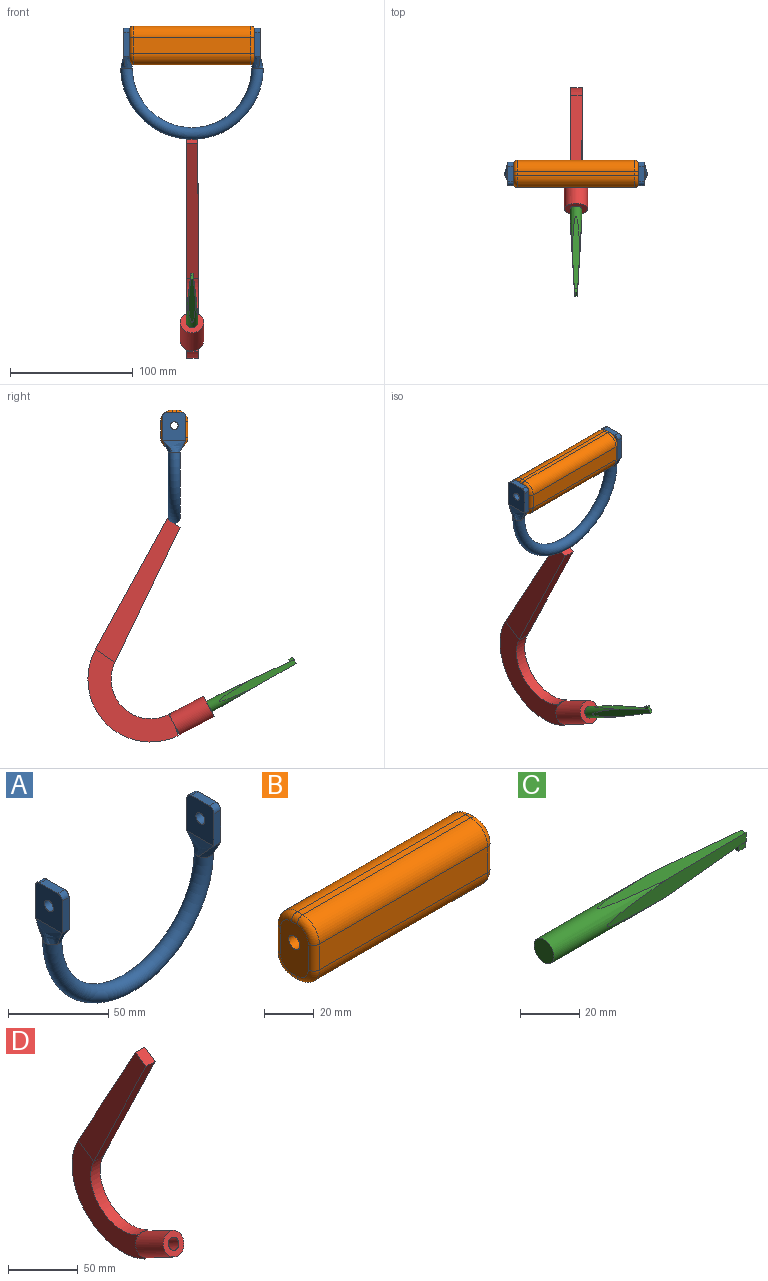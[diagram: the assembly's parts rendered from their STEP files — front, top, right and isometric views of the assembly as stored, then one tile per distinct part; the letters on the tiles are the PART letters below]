
ASSEMBLY  parts=4 mates=2
PART A: 25 faces, bbox 125.8x19.1x95.3 mm
  f0: torus R=53.34mm, axis (0,-1,0), area 5014.4mm2, adj f1,f2,f3,f4,f13,f14,f15,f16
  f1: bspline ~9.53x8.37mm, area 61.9mm2, adj f0,f2,f4,f6
  f2: bspline ~19.05x9.53mm, area 124.7mm2, adj f0,f1,f3,f7
  f3: bspline ~9.53x8.37mm, area 61.9mm2, adj f0,f2,f4,f8
  f4: bspline ~19.05x9.53mm, area 124.7mm2, adj f0,f1,f3,f5
  f5: plane 22.86x19.05mm, normal (1,0,0), area 399.5mm2, adj f4,f6,f8,f9,f10,f11,f12
  f6: plane 19.69x4.76mm, normal (0,1,0), area 93.7mm2, adj f1,f5,f7,f10
  f7: plane 22.86x19.05mm, normal (-1,0,0), area 399.5mm2, adj f2,f6,f8,f9,f10,f11,f12
  f8: plane 19.69x4.76mm, normal (0,-1,0), area 93.7mm2, adj f3,f5,f7,f11
  f9: plane 12.7x4.76mm, normal (0,0,1), area 60.5mm2, adj f5,f7,f10,f11
  f10: cylinder r=3.17mm len=4.76mm, axis (1,0,0), area 23.8mm2, adj f5,f6,f7,f9
  f11: cylinder r=3.17mm len=4.76mm, axis (-1,0,0), area 23.8mm2, adj f5,f7,f8,f9
  f12: cylinder r=3.17mm len=6.35mm, axis (1,0,0), area 95mm2, adj f5,f7
  f13: bspline ~9.53x8.37mm, area 61.9mm2, adj f0,f14,f16,f18
  f14: bspline ~19.05x9.53mm, area 124.7mm2, adj f0,f13,f15,f19
  f15: bspline ~9.53x8.37mm, area 61.9mm2, adj f0,f14,f16,f20
  f16: bspline ~19.05x9.53mm, area 124.7mm2, adj f0,f13,f15,f17
  f17: plane 22.86x19.05mm, normal (-1,0,0), area 399.5mm2, adj f16,f18,f20,f21,f22,f23,f24
  f18: plane 19.69x4.76mm, normal (0,1,0), area 93.7mm2, adj f13,f17,f19,f22
  f19: plane 22.86x19.05mm, normal (1,0,0), area 399.5mm2, adj f14,f18,f20,f21,f22,f23,f24
  f20: plane 19.69x4.76mm, normal (0,-1,0), area 93.7mm2, adj f15,f17,f19,f23
  f21: plane 12.7x4.76mm, normal (0,0,1), area 60.5mm2, adj f17,f19,f22,f23
  f22: cylinder r=3.17mm len=4.76mm, axis (-1,0,0), area 23.8mm2, adj f17,f18,f19,f21
  f23: cylinder r=3.17mm len=4.76mm, axis (1,0,0), area 23.8mm2, adj f17,f19,f20,f21
  f24: cylinder r=3.17mm len=6.35mm, axis (-1,0,0), area 95mm2, adj f17,f19
PART B: 27 faces, bbox 101.9x23.8x33.3 mm
  f0: plane 95.56x12.7mm, normal (0,1,0), area 1213.5mm2, adj f1,f8,f18,f26
  f1: cylinder r=9.53mm len=95.56mm, axis (-1,0,0), area 1429.7mm2, adj f0,f2,f16,f24
  f2: plane 95.56x3.18mm, normal (0,0,1), area 303.4mm2, adj f1,f3,f14,f22
  f3: cylinder r=9.53mm len=95.56mm, axis (-1,0,0), area 1429.7mm2, adj f2,f4,f12,f20
  f4: plane 95.56x12.7mm, normal (0,-1,0), area 1213.5mm2, adj f3,f5,f11,f19
  f5: cylinder r=9.53mm len=95.56mm, axis (-1,0,0), area 1429.7mm2, adj f4,f6,f13,f21
  f6: plane 95.56x3.18mm, normal (0,0,-1), area 303.4mm2, adj f5,f8,f15,f23
  f7: cylinder r=3.17mm len=101.91mm, axis (-1,0,0), area 2032.9mm2, adj f9,f10
  f8: cylinder r=9.53mm len=95.56mm, axis (-1,0,0), area 1429.7mm2, adj f0,f6,f17,f25
  f9: plane 25.4x15.88mm, normal (1,0,0), area 336.9mm2, adj f7,f19,f20,f21,f22,f23,f24,f25
  f10: plane 25.4x15.88mm, normal (-1,0,0), area 336.9mm2, adj f7,f11,f12,f13,f14,f15,f16,f17
  f11: cylinder r=3.17mm len=12.7mm, axis (0,0,-1), area 63.3mm2, adj f4,f10,f12,f13
  f12: torus R=6.35mm, axis (1,0,0), area 65.6mm2, adj f3,f10,f11,f14
  f13: torus R=6.35mm, axis (1,0,0), area 65.6mm2, adj f5,f10,f11,f15
  f14: cylinder r=3.17mm len=3.18mm, axis (0,-1,0), area 15.8mm2, adj f2,f10,f12,f16
  f15: cylinder r=3.17mm len=3.18mm, axis (0,1,0), area 15.8mm2, adj f6,f10,f13,f17
  f16: torus R=6.35mm, axis (1,0,0), area 65.6mm2, adj f1,f10,f14,f18
  f17: torus R=6.35mm, axis (1,0,0), area 65.6mm2, adj f8,f10,f15,f18
  f18: cylinder r=3.17mm len=12.7mm, axis (0,0,1), area 63.3mm2, adj f0,f10,f16,f17
  f19: cylinder r=3.17mm len=12.7mm, axis (0,0,1), area 63.3mm2, adj f4,f9,f20,f21
  f20: torus R=6.35mm, axis (1,0,0), area 65.6mm2, adj f3,f9,f19,f22
  f21: torus R=6.35mm, axis (1,0,0), area 65.6mm2, adj f5,f9,f19,f23
  f22: cylinder r=3.17mm len=3.18mm, axis (0,1,0), area 15.8mm2, adj f2,f9,f20,f24
  f23: cylinder r=3.17mm len=3.18mm, axis (0,-1,0), area 15.8mm2, adj f6,f9,f21,f25
  f24: torus R=6.35mm, axis (1,0,0), area 65.6mm2, adj f1,f9,f22,f26
  f25: torus R=6.35mm, axis (1,0,0), area 65.6mm2, adj f8,f9,f23,f26
  f26: cylinder r=3.17mm len=12.7mm, axis (0,0,-1), area 63.3mm2, adj f0,f9,f24,f25
PART C: 12 faces, bbox 95.3x9.5x9.5 mm
  f0: plane 69.85x6.44mm, normal (0.04,0,-1), area 295.5mm2, adj f2,f3,f4,f5,f6,f7,f8,f9
  f1: plane 69.85x6.44mm, normal (0.04,0,1), area 303.5mm2, adj f2,f3,f4,f5
  f2: plane 69.85x7.02mm, normal (0.05,1,0), area 356.8mm2, adj f0,f1,f4,f5
  f3: plane 69.85x7.02mm, normal (0.05,-1,0), area 356.8mm2, adj f0,f1,f4,f5
  f4: plane 3.53x2.13mm, normal (1,0,0), area 7.5mm2, adj f0,f1,f2,f3
  f5: cylinder r=4.76mm len=54.58mm, axis (-1,0,0), area 1057.3mm2, adj f0,f1,f2,f3,f11
  f6: plane 2.5x2.08mm, normal (-1,0,0.04), area 5.2mm2, adj f0,f7,f9,f10
  f7: plane 3.53x2.38mm, normal (0.05,-1,0), area 7.7mm2, adj f0,f6,f8,f10
  f8: plane 2.38x2.13mm, normal (1,0,-0.04), area 5.1mm2, adj f0,f7,f9,f10
  f9: plane 3.53x2.38mm, normal (0.05,1,0), area 7.7mm2, adj f0,f6,f8,f10
  f10: plane 3.43x2.5mm, normal (-0.04,0,-1), area 7.9mm2, adj f6,f7,f8,f9
  f11: plane 9.53x9.53mm, normal (-1,0,0), area 71.3mm2, adj f5
PART D: 18 faces, bbox 19.1x103x182.3 mm
  f0: plane 3.87x1.33mm, normal (0,-0.94,0.34), area 2.1mm2, adj f8,f9,f13
  f1: plane 3.18x0.95mm, normal (0,-0.94,0.34), area 1.3mm2, adj f9,f10,f13
  f2: plane 10.4x9.53mm, normal (0,-0.57,0.82), area 121mm2, adj f3,f4,f5,f6
  f3: plane 117.35x68.76mm, normal (1,0,0), area 1915.3mm2, adj f2,f4,f6,f8
  f4: plane 106.43x58.36mm, normal (0,0.88,0.48), area 1156.1mm2, adj f2,f3,f5,f11
  f5: plane 117.35x68.76mm, normal (-1,0,0), area 1915.3mm2, adj f2,f4,f6,f10
  f6: plane 110.07x53.15mm, normal (0,-0.9,-0.43), area 1164.2mm2, adj f2,f3,f5,f9
  f7: plane 9.53x8.94mm, normal (0,-0.94,0.34), area 90.7mm2, adj f8,f10,f11,f15
  f8: plane 75.84x73.7mm, normal (1,0,0), area 1989.1mm2, adj f0,f3,f7,f9,f11,f13,f15
  f9: cylinder r=32.24mm len=48.27mm, axis (-1,0,0), area 774.5mm2, adj f0,f1,f6,f8,f10,f12,f13
  f10: plane 75.84x73.7mm, normal (-1,0,0), area 1988.6mm2, adj f1,f5,f7,f9,f11,f13,f15
  f11: cylinder r=51.12mm len=75.84mm, axis (-1,0,0), area 1233.4mm2, adj f4,f7,f8,f10
  f12: plane 2.82x0.09mm, normal (0,0.89,-0.46), area 0.2mm2, adj f9,f13
  f13: cylinder r=9.53mm len=36.96mm, axis (0,0.89,-0.46), area 1891.6mm2, adj f0,f1,f8,f9,f10,f12,f14,f15
  f14: plane 19.05x16.88mm, normal (0,-0.89,0.46), area 213.8mm2, adj f13,f16
  f15: plane 19.05x15.92mm, normal (0,0.89,-0.46), area 198.3mm2, adj f7,f8,f10,f13
  f16: cylinder r=4.76mm len=26.92mm, axis (0,-0.89,0.46), area 760.1mm2, adj f14,f17
  f17: plane 9.53x8.44mm, normal (0,-0.89,0.46), area 71.3mm2, adj f16
PLACE A t=(0,336.28,-4.09)mm
PLACE B t=(0.01,336.28,14.32)mm
PLACE C rot(axis=(0.7,-0.7,0.17),160.6deg) t=(0,299.7,-207.16)mm
PLACE D t=(0,336.28,-4.09)mm
MATE fastened B.f7 <-> A.f12  axis (1,0,0) through (50.96,336.28,17.5)mm
MATE fastened C.f5 <-> D.f16  axis (0,0.89,-0.46) through (0,322.21,-218.92)mm
